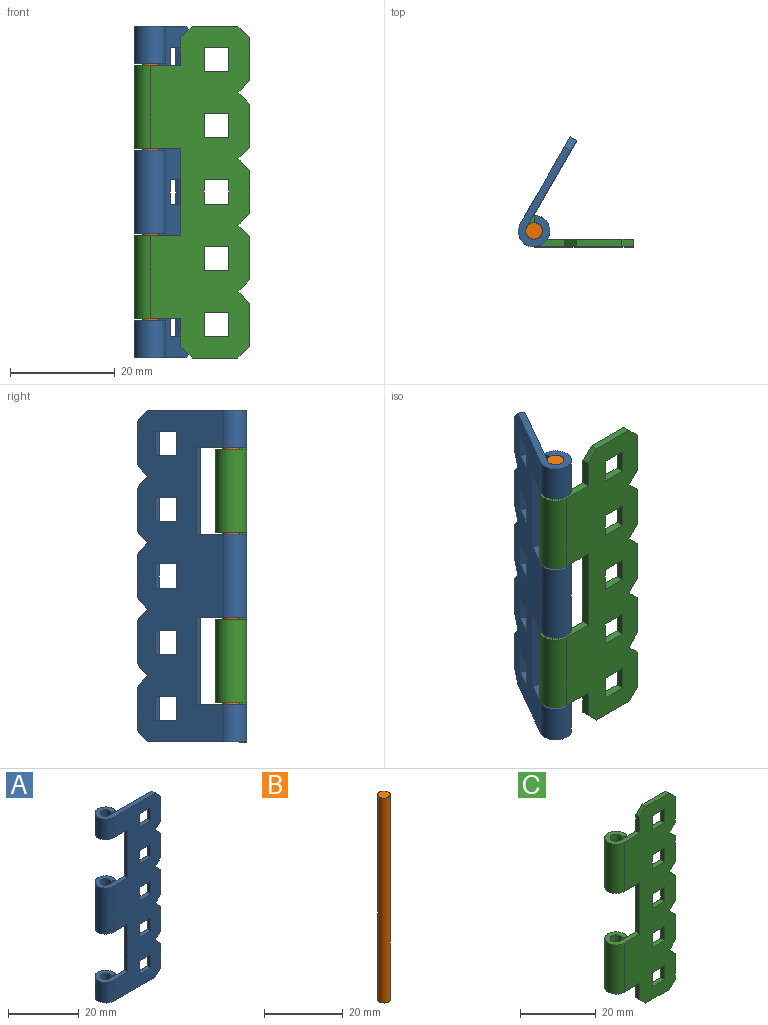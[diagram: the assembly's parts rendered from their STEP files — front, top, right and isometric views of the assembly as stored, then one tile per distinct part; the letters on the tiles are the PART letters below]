
ASSEMBLY  parts=3 mates=2
PART A: 54 faces, bbox 22x6x63.5 mm
  f0: cylinder r=2.98mm len=7.12mm, axis (0,0,1), area 111.3mm2, adj f7,f40,f41,f48
  f1: cylinder r=1.59mm len=7.12mm, axis (0,0,1), area 59.2mm2, adj f6,f40,f41,f48
  f2: cylinder r=2.98mm len=15.88mm, axis (0,0,1), area 248.1mm2, adj f7,f44,f45,f47
  f3: cylinder r=1.59mm len=15.88mm, axis (0,0,1), area 132mm2, adj f6,f44,f45,f47
  f4: cylinder r=2.98mm len=7.12mm, axis (0,0,1), area 111.3mm2, adj f7,f42,f43,f46
  f5: cylinder r=1.59mm len=7.12mm, axis (0,0,1), area 59.2mm2, adj f6,f42,f43,f46
  f6: plane 63.5x19.05mm, normal (0,1,0), area 882.3mm2, adj f1,f3,f5,f8,f9,f10,f11,f12
  f7: plane 63.5x19.05mm, normal (0,-1,0), area 882.3mm2, adj f0,f2,f4,f8,f9,f10,f11,f12
  f8: plane 2.25x2.25mm, normal (0.71,0,0.71), area 4.4mm2, adj f6,f7,f40,f49
  f9: plane 16.69x1.4mm, normal (-1,0,0), area 23.3mm2, adj f6,f7,f41,f44
  f10: plane 16.69x1.4mm, normal (-1,0,0), area 23.3mm2, adj f6,f7,f42,f45
  f11: plane 2.25x2.25mm, normal (0.71,0,-0.71), area 4.4mm2, adj f6,f7,f43,f50
  f12: plane 4.62x1.4mm, normal (1,0,0), area 6.5mm2, adj f6,f7,f13,f15
  f13: plane 4.62x1.4mm, normal (0,0,-1), area 6.5mm2, adj f6,f7,f12,f14
  f14: plane 4.62x1.4mm, normal (-1,0,0), area 6.5mm2, adj f6,f7,f13,f15
  f15: plane 4.62x1.4mm, normal (0,0,1), area 6.5mm2, adj f6,f7,f12,f14
  f16: plane 4.62x1.4mm, normal (1,0,0), area 6.5mm2, adj f6,f7,f17,f19
  f17: plane 4.62x1.4mm, normal (0,0,-1), area 6.5mm2, adj f6,f7,f16,f18
  f18: plane 4.62x1.4mm, normal (-1,0,0), area 6.5mm2, adj f6,f7,f17,f19
  f19: plane 4.62x1.4mm, normal (0,0,1), area 6.5mm2, adj f6,f7,f16,f18
  f20: plane 4.62x1.4mm, normal (1,0,0), area 6.5mm2, adj f6,f7,f21,f23
  f21: plane 4.62x1.4mm, normal (0,0,-1), area 6.5mm2, adj f6,f7,f20,f22
  f22: plane 4.62x1.4mm, normal (-1,0,0), area 6.5mm2, adj f6,f7,f21,f23
  f23: plane 4.62x1.4mm, normal (0,0,1), area 6.5mm2, adj f6,f7,f20,f22
  f24: plane 4.62x1.4mm, normal (1,0,0), area 6.5mm2, adj f6,f7,f25,f27
  f25: plane 4.62x1.4mm, normal (0,0,-1), area 6.5mm2, adj f6,f7,f24,f26
  f26: plane 4.62x1.4mm, normal (-1,0,0), area 6.5mm2, adj f6,f7,f25,f27
  f27: plane 4.62x1.4mm, normal (0,0,1), area 6.5mm2, adj f6,f7,f24,f26
  f28: plane 4.62x1.4mm, normal (1,0,0), area 6.5mm2, adj f6,f7,f29,f31
  f29: plane 4.62x1.4mm, normal (0,0,-1), area 6.5mm2, adj f6,f7,f28,f30
  f30: plane 4.62x1.4mm, normal (-1,0,0), area 6.5mm2, adj f6,f7,f29,f31
  f31: plane 4.62x1.4mm, normal (0,0,1), area 6.5mm2, adj f6,f7,f28,f30
  f32: plane 2.25x2.25mm, normal (0.71,0,0.71), area 4.4mm2, adj f6,f7,f33,f53
  f33: plane 2.25x2.25mm, normal (0.71,0,-0.71), area 4.4mm2, adj f6,f7,f32,f49
  f34: plane 2.25x2.25mm, normal (0.71,0,0.71), area 4.4mm2, adj f6,f7,f35,f52
  f35: plane 2.25x2.25mm, normal (0.71,0,-0.71), area 4.4mm2, adj f6,f7,f34,f53
  f36: plane 2.25x2.25mm, normal (0.71,0,0.71), area 4.4mm2, adj f6,f7,f37,f51
  f37: plane 2.25x2.25mm, normal (0.71,0,-0.71), area 4.4mm2, adj f6,f7,f36,f52
  f38: plane 2.25x2.25mm, normal (0.71,0,0.71), area 4.4mm2, adj f6,f7,f39,f50
  f39: plane 2.25x2.25mm, normal (0.71,0,-0.71), area 4.4mm2, adj f6,f7,f38,f51
  f40: plane 19.79x5.97mm, normal (0,0,1), area 40.2mm2, adj f0,f1,f6,f7,f8,f48
  f41: plane 8.84x5.97mm, normal (0,0,-1), area 24.9mm2, adj f0,f1,f6,f7,f9,f48
  f42: plane 8.84x5.97mm, normal (0,0,1), area 24.9mm2, adj f4,f5,f6,f7,f10,f46
  f43: plane 19.79x5.97mm, normal (0,0,-1), area 40.2mm2, adj f4,f5,f6,f7,f11,f46
  f44: plane 8.84x5.97mm, normal (0,0,1), area 24.9mm2, adj f2,f3,f6,f7,f9,f47
  f45: plane 8.84x5.97mm, normal (0,0,-1), area 24.9mm2, adj f2,f3,f6,f7,f10,f47
  f46: plane 7.12x1.21mm, normal (-0.5,-0.87,0), area 10mm2, adj f4,f5,f42,f43
  f47: plane 15.88x1.21mm, normal (-0.5,-0.87,0), area 22.2mm2, adj f2,f3,f44,f45
  f48: plane 7.12x1.21mm, normal (-0.5,-0.87,0), area 10mm2, adj f0,f1,f40,f41
  f49: plane 8.21x1.4mm, normal (1,0,0), area 11.5mm2, adj f6,f7,f8,f33
  f50: plane 8.21x1.4mm, normal (1,0,0), area 11.5mm2, adj f6,f7,f11,f38
  f51: plane 8.21x1.4mm, normal (1,0,0), area 11.5mm2, adj f6,f7,f36,f39
  f52: plane 8.21x1.4mm, normal (1,0,0), area 11.5mm2, adj f6,f7,f34,f37
  f53: plane 8.21x1.4mm, normal (1,0,0), area 11.5mm2, adj f6,f7,f32,f35
PART B: 3 faces, bbox 3.2x3.2x63.5 mm
  f0: cylinder r=1.59mm len=63.5mm, axis (0,0,-1), area 633.4mm2, adj f1,f2
  f1: plane 3.18x3.18mm, normal (0,0,1), area 7.9mm2, adj f0
  f2: plane 3.18x3.18mm, normal (0,0,-1), area 7.9mm2, adj f0
PART C: 54 faces, bbox 22.1x6x63.5 mm
  f0: cylinder r=3.01mm len=15.88mm, axis (0,0,1), area 250.2mm2, adj f5,f43,f44,f48
  f1: cylinder r=1.59mm len=15.88mm, axis (0,0,1), area 132mm2, adj f4,f43,f44,f48
  f2: cylinder r=3.01mm len=15.88mm, axis (0,0,1), area 250.2mm2, adj f5,f45,f46,f47
  f3: cylinder r=1.59mm len=15.88mm, axis (0,0,1), area 132mm2, adj f4,f45,f46,f47
  f4: plane 63.5x19.05mm, normal (0,1,0), area 888.2mm2, adj f1,f3,f6,f7,f8,f9,f10,f11
  f5: plane 63.5x19.05mm, normal (0,-1,0), area 888.2mm2, adj f0,f2,f6,f7,f8,f9,f10,f11
  f6: plane 16.69x1.42mm, normal (-1,0,0), area 23.7mm2, adj f4,f5,f44,f45
  f7: plane 5.29x1.42mm, normal (-1,0,0), area 7.5mm2, adj f4,f5,f8,f46
  f8: plane 2.25x2.25mm, normal (-0.71,0,-0.71), area 4.5mm2, adj f4,f5,f7,f9
  f9: plane 8.75x1.42mm, normal (0,0,-1), area 12.4mm2, adj f4,f5,f8,f10
  f10: plane 2.25x2.25mm, normal (0.71,0,-0.71), area 4.5mm2, adj f4,f5,f9,f50
  f11: plane 2.25x2.25mm, normal (0.71,0,0.71), area 4.5mm2, adj f4,f5,f12,f49
  f12: plane 8.75x1.42mm, normal (0,0,1), area 12.4mm2, adj f4,f5,f11,f13
  f13: plane 2.25x2.25mm, normal (-0.71,0,0.71), area 4.5mm2, adj f4,f5,f12,f14
  f14: plane 5.29x1.42mm, normal (-1,0,0), area 7.5mm2, adj f4,f5,f13,f43
  f15: plane 4.62x1.42mm, normal (1,0,0), area 6.6mm2, adj f4,f5,f16,f18
  f16: plane 4.62x1.42mm, normal (0,0,-1), area 6.6mm2, adj f4,f5,f15,f17
  f17: plane 4.62x1.42mm, normal (-1,0,0), area 6.6mm2, adj f4,f5,f16,f18
  f18: plane 4.62x1.42mm, normal (0,0,1), area 6.6mm2, adj f4,f5,f15,f17
  f19: plane 4.62x1.42mm, normal (1,0,0), area 6.6mm2, adj f4,f5,f20,f22
  f20: plane 4.62x1.42mm, normal (0,0,-1), area 6.6mm2, adj f4,f5,f19,f21
  f21: plane 4.62x1.42mm, normal (-1,0,0), area 6.6mm2, adj f4,f5,f20,f22
  f22: plane 4.62x1.42mm, normal (0,0,1), area 6.6mm2, adj f4,f5,f19,f21
  f23: plane 4.62x1.42mm, normal (1,0,0), area 6.6mm2, adj f4,f5,f24,f26
  f24: plane 4.62x1.42mm, normal (0,0,-1), area 6.6mm2, adj f4,f5,f23,f25
  f25: plane 4.62x1.42mm, normal (-1,0,0), area 6.6mm2, adj f4,f5,f24,f26
  f26: plane 4.62x1.42mm, normal (0,0,1), area 6.6mm2, adj f4,f5,f23,f25
  f27: plane 4.62x1.42mm, normal (1,0,0), area 6.6mm2, adj f4,f5,f28,f30
  f28: plane 4.62x1.42mm, normal (0,0,-1), area 6.6mm2, adj f4,f5,f27,f29
  f29: plane 4.62x1.42mm, normal (-1,0,0), area 6.6mm2, adj f4,f5,f28,f30
  f30: plane 4.62x1.42mm, normal (0,0,1), area 6.6mm2, adj f4,f5,f27,f29
  f31: plane 4.62x1.42mm, normal (1,0,0), area 6.6mm2, adj f4,f5,f32,f34
  f32: plane 4.62x1.42mm, normal (0,0,-1), area 6.6mm2, adj f4,f5,f31,f33
  f33: plane 4.62x1.42mm, normal (-1,0,0), area 6.6mm2, adj f4,f5,f32,f34
  f34: plane 4.62x1.42mm, normal (0,0,1), area 6.6mm2, adj f4,f5,f31,f33
  f35: plane 2.25x2.25mm, normal (0.71,0,0.71), area 4.5mm2, adj f4,f5,f36,f53
  f36: plane 2.25x2.25mm, normal (0.71,0,-0.71), area 4.5mm2, adj f4,f5,f35,f49
  f37: plane 2.25x2.25mm, normal (0.71,0,0.71), area 4.5mm2, adj f4,f5,f38,f52
  f38: plane 2.25x2.25mm, normal (0.71,0,-0.71), area 4.5mm2, adj f4,f5,f37,f53
  f39: plane 2.25x2.25mm, normal (0.71,0,0.71), area 4.5mm2, adj f4,f5,f40,f51
  f40: plane 2.25x2.25mm, normal (0.71,0,-0.71), area 4.5mm2, adj f4,f5,f39,f52
  f41: plane 2.25x2.25mm, normal (0.71,0,0.71), area 4.5mm2, adj f4,f5,f42,f50
  f42: plane 2.25x2.25mm, normal (0.71,0,-0.71), area 4.5mm2, adj f4,f5,f41,f51
  f43: plane 8.82x6.02mm, normal (0,0,1), area 25.4mm2, adj f0,f1,f4,f5,f14,f48
  f44: plane 8.82x6.02mm, normal (0,0,-1), area 25.4mm2, adj f0,f1,f4,f5,f6,f48
  f45: plane 8.82x6.02mm, normal (0,0,1), area 25.4mm2, adj f2,f3,f4,f5,f6,f47
  f46: plane 8.82x6.02mm, normal (0,0,-1), area 25.4mm2, adj f2,f3,f4,f5,f7,f47
  f47: plane 15.88x1.23mm, normal (-0.5,-0.87,0), area 22.6mm2, adj f2,f3,f45,f46
  f48: plane 15.88x1.23mm, normal (-0.5,-0.87,0), area 22.6mm2, adj f0,f1,f43,f44
  f49: plane 8.21x1.42mm, normal (1,0,0), area 11.7mm2, adj f4,f5,f11,f36
  f50: plane 8.21x1.42mm, normal (1,0,0), area 11.7mm2, adj f4,f5,f10,f41
  f51: plane 8.21x1.42mm, normal (1,0,0), area 11.7mm2, adj f4,f5,f39,f42
  f52: plane 8.21x1.42mm, normal (1,0,0), area 11.7mm2, adj f4,f5,f37,f40
  f53: plane 8.21x1.42mm, normal (1,0,0), area 11.7mm2, adj f4,f5,f35,f38
PLACE A rot(axis=(0.87,0.5,0),180deg) t=(-12.57,15.75,1.67)mm
PLACE B t=(-17.92,0.51,-30.08)mm
PLACE C t=(-2.04,-2.5,1.67)mm
MATE fastened B.f0 <-> C.f0  axis (0,0,1) through (-17.92,0.51,33.42)mm
MATE revolute A.f0 <-> B.f0  axis (0,0,1) through (-17.92,0.51,33.42)mm
